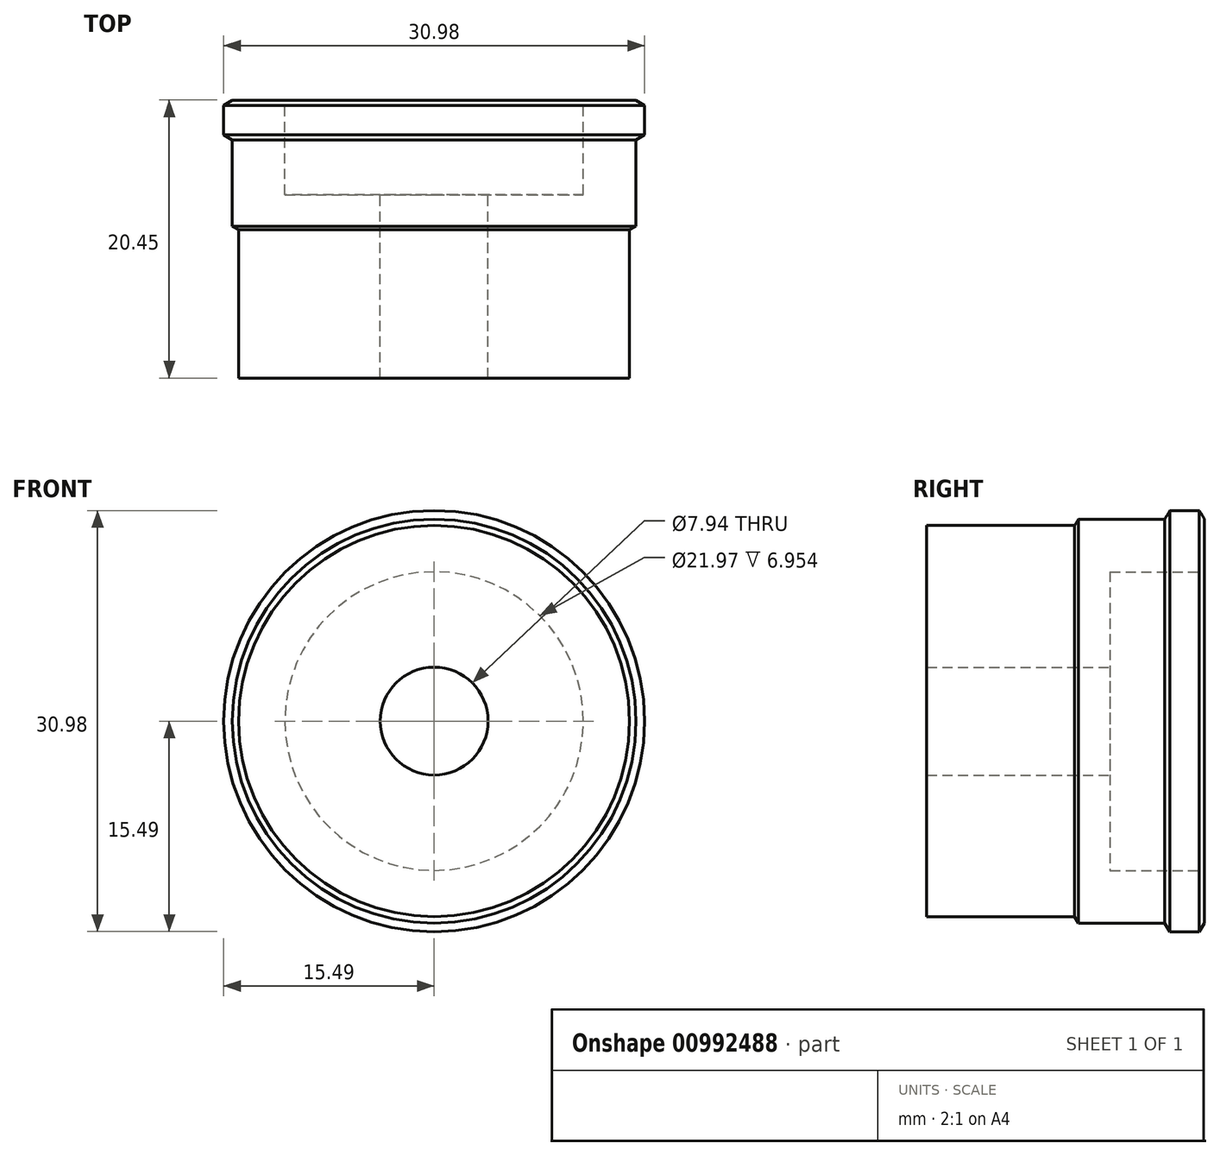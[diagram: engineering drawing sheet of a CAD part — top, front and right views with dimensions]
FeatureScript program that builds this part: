
annotation { "Feature Type Name" : "Feature", "Feature Type Description" : "" }
export const myFeature = defineFeature(function(context is Context, id is Id, definition is map)
    precondition{}
    {
        {
            var Q0;
            Q0=qCreatedBy(makeId("Right.planeOp"),FACE);
            var sketch = newSketch(context, id + "F0", { "sketchPlane" : qUnion([Q0])});
            skLineSegment(sketch, "E0", {"start": v(0, 14.39) * mm, "end": v(10.9, 14.39) * mm});
            skLineSegment(sketch, "E1", {"start": v(10.9, 14.39) * mm, "end": v(11.18, 14.86) * mm});
            skLineSegment(sketch, "E2", {"start": v(11.18, 14.86) * mm, "end": v(17.53, 14.86) * mm});
            skLineSegment(sketch, "E3", {"start": v(17.53, 14.86) * mm, "end": v(17.9, 15.5) * mm});
            skLineSegment(sketch, "E4", {"start": v(17.9, 15.5) * mm, "end": v(20.07, 15.5) * mm});
            skLineSegment(sketch, "E5", {"start": v(20.07, 15.5) * mm, "end": v(20.45, 14.86) * mm});
            skLineSegment(sketch, "E6", {"start": v(20.45, 14.86) * mm, "end": v(20.45, 10.99) * mm});
            skLineSegment(sketch, "E7", {"start": v(20.45, 0) * mm, "end": v(0, 0) * mm, "construction": true});
            skLineSegment(sketch, "E8", {"start": v(0, 3.97) * mm, "end": v(0, 14.39) * mm});
            skLineSegment(sketch, "E9", {"start": v(20.45, 14.86) * mm, "end": v(20.45, 18.7) * mm, "construction": true});
            skLineSegment(sketch, "E10", {"start": v(17.53, 14.86) * mm, "end": v(17.53, 17) * mm, "construction": true});
            skLineSegment(sketch, "E11", {"start": v(11.18, 14.86) * mm, "end": v(11.18, 12.99) * mm, "construction": true});
            skLineSegment(sketch, "E12", {"start": v(13.5, 10.99) * mm, "end": v(13.5, 3.97) * mm});
            skLineSegment(sketch, "E13", {"start": v(13.5, 3.97) * mm, "end": v(0, 3.97) * mm});
            skLineSegment(sketch, "E14", {"start": v(20.45, 10.99) * mm, "end": v(13.5, 10.99) * mm});
            skSolve(sketch);
        }
        {
            var Q0;
            Q0 = qSketchRegion(id + "F0", true);
            var Q1;
            Q1=sQuery(id+"F0.wireOp",EDGE,"E7");
            revolve(context, id + "F1", {"surfaceOperationType" : NewSurfaceOperationType.NEW, "entities" : qUnion([Q0]), "axis" : qUnion([Q1]), "revolveType" : RevolveType.FULL});
        }
    });
